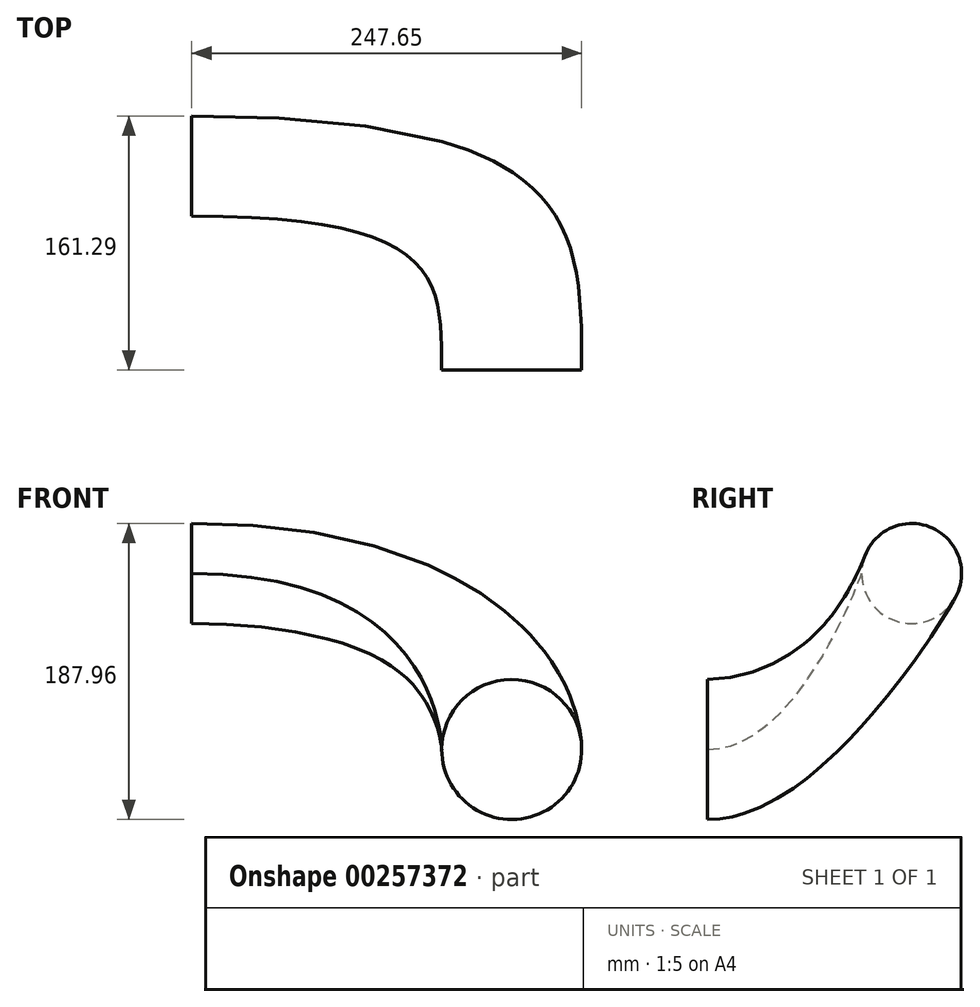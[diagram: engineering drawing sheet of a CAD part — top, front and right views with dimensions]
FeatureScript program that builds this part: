
annotation { "Feature Type Name" : "Feature", "Feature Type Description" : "" }
export const myFeature = defineFeature(function(context is Context, id is Id, definition is map)
    precondition{}
    {
        {
            var Q0;
            Q0=qCreatedBy(makeId("Right.planeOp"),FACE);
            cPlane(context, id + "F0", {"entities" : qUnion([Q0]), "cplaneType" : CPlaneType.OFFSET, "offset" : 203.2 * mm, "oppositeDirection" : true, "width" : 152.4 * mm, "height" : 152.4 * mm});
        }
        {
            var Q0;
            Q0=qCreatedBy(makeId("Top.planeOp"),FACE);
            cPlane(context, id + "F1", {"entities" : qUnion([Q0]), "cplaneType" : CPlaneType.OFFSET, "offset" : 111.76 * mm, "width" : 152.4 * mm, "height" : 152.4 * mm});
        }
        {
            var Q0;
            Q0=qCreatedBy(makeId("Front.planeOp"),FACE);
            var sketch = newSketch(context, id + "F2", { "sketchPlane" : qUnion([Q0])});
            skCircle(sketch, "E0", {"center": v(0, 0) * mm, "radius": 44.45 * mm});
            skSolve(sketch);
        }
        {
            var Q0;
            Q0=qCreatedBy(id+"F0.planeOp",FACE);
            var sketch = newSketch(context, id + "F3", { "sketchPlane" : qUnion([Q0])});
            skCircle(sketch, "E1", {"center": v(129.54, 111.76) * mm, "radius": 31.75 * mm});
            skCircle(sketch, "E2.1.0.0", {"center": v(241.3, 111.76) * mm, "radius": 31.75 * mm});
            skCircle(sketch, "E2.2.0.0", {"center": v(353.06, 111.76) * mm, "radius": 31.75 * mm});
            skCircle(sketch, "E2.3.0.0", {"center": v(464.82, 111.76) * mm, "radius": 31.75 * mm});
            skLineSegment(sketch, "E2.direction1", {"start": v(129.54, 111.76) * mm, "end": v(241.3, 111.76) * mm, "construction": true});
            skSolve(sketch);
        }
        {
            var Q0;
            Q0=qCreatedBy(id+"F1.planeOp",FACE);
            var sketch = newSketch(context, id + "F4", { "sketchPlane" : qUnion([Q0])});
            skLineSegment(sketch, "E3", {"start": v(-203.2, 97.8) * mm, "end": v(-203.2, 209.55) * mm, "construction": true});
            skLineSegment(sketch, "E4", {"start": v(-203.2, 97.8) * mm, "end": v(-177.8, 97.8) * mm, "construction": true});
            skLineSegment(sketch, "E5.0.1.0", {"start": v(-203.2, 209.55) * mm, "end": v(-203.2, 321.31) * mm, "construction": true});
            skLineSegment(sketch, "E5.0.1.1", {"start": v(-203.2, 209.55) * mm, "end": v(-177.8, 209.55) * mm, "construction": true});
            skLineSegment(sketch, "E5.0.2.0", {"start": v(-203.2, 321.31) * mm, "end": v(-203.2, 433.07) * mm, "construction": true});
            skLineSegment(sketch, "E5.0.2.1", {"start": v(-203.2, 321.31) * mm, "end": v(-177.8, 321.31) * mm, "construction": true});
            skLineSegment(sketch, "E5.1.1.0", {"start": v(-203.2, 209.55) * mm, "end": v(-203.2, 321.31) * mm, "construction": true});
            skLineSegment(sketch, "E5.1.1.1", {"start": v(-203.2, 209.55) * mm, "end": v(-177.8, 209.55) * mm, "construction": true});
            skLineSegment(sketch, "E5.1.2.0", {"start": v(-203.2, 321.31) * mm, "end": v(-203.2, 433.07) * mm, "construction": true});
            skLineSegment(sketch, "E5.1.2.1", {"start": v(-203.2, 321.31) * mm, "end": v(-177.8, 321.31) * mm, "construction": true});
            skLineSegment(sketch, "E5.2.1.0", {"start": v(-203.2, 209.55) * mm, "end": v(-203.2, 321.31) * mm, "construction": true});
            skLineSegment(sketch, "E5.2.1.1", {"start": v(-203.2, 209.55) * mm, "end": v(-177.8, 209.55) * mm, "construction": true});
            skLineSegment(sketch, "E5.2.2.0", {"start": v(-203.2, 321.31) * mm, "end": v(-203.2, 433.07) * mm, "construction": true});
            skLineSegment(sketch, "E5.2.2.1", {"start": v(-203.2, 321.31) * mm, "end": v(-177.8, 321.31) * mm, "construction": true});
            skLineSegment(sketch, "E5.direction1", {"start": v(-203.2, 97.8) * mm, "end": v(-203.2, 97.8) * mm});
            skLineSegment(sketch, "E6", {"start": v(-203.2, 433.07) * mm, "end": v(-177.8, 433.07) * mm, "construction": true});
            skSolve(sketch);
        }
        {
            var Q0;
            Q0=qCreatedBy(makeId("Top.planeOp"),FACE);
            var sketch = newSketch(context, id + "F5", { "sketchPlane" : qUnion([Q0])});
            skLineSegment(sketch, "E7", {"start": v(44.45, 0) * mm, "end": v(-44.45, 0) * mm, "construction": true});
            skLineSegment(sketch, "E8", {"start": v(-44.45, 0) * mm, "end": v(-44.45, 8.03) * mm});
            skLineSegment(sketch, "E9", {"start": v(-44.45, 8.03) * mm, "end": v(-44.45, 25.4) * mm});
            skPoint(sketch, "E10", {"position": v(-44.45, 8.03) * mm});
            skSolve(sketch);
        }
        {
            var Q0;
            Q0=qCreatedBy(makeId("Front.planeOp"),FACE);
            cPlane(context, id + "F6", {"entities" : qUnion([Q0]), "cplaneType" : CPlaneType.OFFSET, "offset" : 76.2 * mm, "oppositeDirection" : true, "width" : 152.4 * mm, "height" : 152.4 * mm});
        }
        {
            var Q0;
            Q0=qCreatedBy(makeId("Right.planeOp"),FACE);
            cPlane(context, id + "F7", {"entities" : qUnion([Q0]), "cplaneType" : CPlaneType.OFFSET, "offset" : 76.2 * mm, "oppositeDirection" : true, "width" : 152.4 * mm, "height" : 152.4 * mm});
        }
        {
            var Q0;
            Q0=makeQuery(id+"F2.imprint","IMPRINT",FACE,{"disambiguationData":[TD([[makeQuery(id+"F2.imprint","IMPRINT",EDGE,{"derivedFrom":sQuery(id+"F2.wireOp",EDGE,"E0")}),1.0]])]});
            var Q1;
            Q1=makeQuery(id+"F3.imprint","IMPRINT",FACE,{"disambiguationData":[TD([[makeQuery(id+"F3.imprint","IMPRINT",EDGE,{"derivedFrom":sQuery(id+"F3.wireOp",EDGE,"E1")}),1.0]])]});
            var Q2;
            Q2=sQuery(id+"F5.wireOp",VERTEX,"E8.start");
            var Q3;
            Q3=sQuery(id+"F4.wireOp",VERTEX,"E4.start");
            loft(context, id + "F8", {"startCondition" : LoftEndDerivativeType.NORMAL_TO_PROFILE, "startMagnitude" : 1.6, "endCondition" : LoftEndDerivativeType.NORMAL_TO_PROFILE, "endMagnitude" : 2.9, "sheetProfilesArray" : [{ "sheetProfileEntities" : qUnion([Q0]) }, { "sheetProfileEntities" : qUnion([Q1]) }], "matchConnections" : true, "connections" : [{ "connectionEntities" : qUnion([Q2, Q3]), "connectionEdgeQueries" : qUnion([]), "connectionEdgeParameters" : [] }]});
        }
    });
